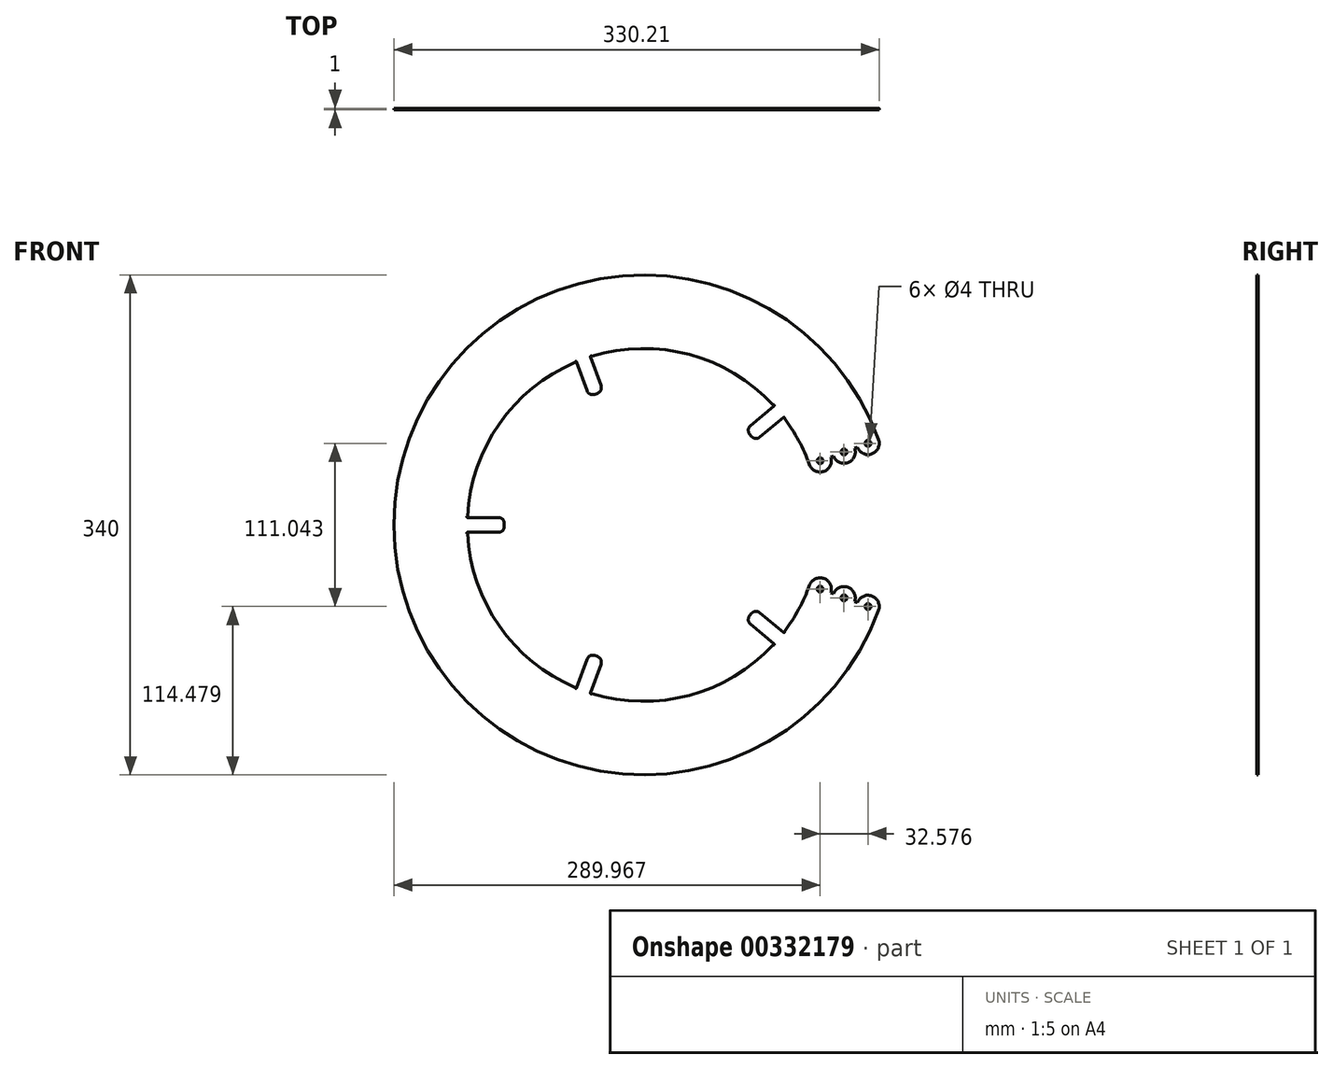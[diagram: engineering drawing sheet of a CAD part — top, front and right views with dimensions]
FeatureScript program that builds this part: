
annotation { "Feature Type Name" : "Feature", "Feature Type Description" : "" }
export const myFeature = defineFeature(function(context is Context, id is Id, definition is map)
    precondition{}
    {
        {
            var Q0;
            Q0=qCreatedBy(makeId("Front.planeOp"),FACE);
            var sketch = newSketch(context, id + "F0", { "sketchPlane" : qUnion([Q0])});
            skArc(sketch, "E0", {"start": v(112.76, 41.04) * mm, "mid": v(105.4, 57.38) * mm, "end": v(95.67, 72.44) * mm});
            skArc(sketch, "E1", {"start": v(159.75, 58.14) * mm, "mid": v(-170, 0) * mm, "end": v(159.75, -58.14) * mm});
            skLineSegment(sketch, "E2", {"start": v(0, 0) * mm, "end": v(-170, 0) * mm, "construction": true});
            skLineSegment(sketch, "E3", {"start": v(0, 0) * mm, "end": v(112.76, 41.04) * mm, "construction": true});
            skLineSegment(sketch, "E4", {"start": v(159.75, 58.14) * mm, "end": v(112.76, 41.04) * mm, "construction": true});
            skArc(sketch, "E5", {"start": v(112.76, 41.04) * mm, "mid": v(122.59, 36.46) * mm, "end": v(127.17, 46.29) * mm});
            skArc(sketch, "E6", {"start": v(129.05, 46.97) * mm, "mid": v(138.88, 42.39) * mm, "end": v(143.46, 52.22) * mm});
            skArc(sketch, "E7", {"start": v(159.75, 58.14) * mm, "mid": v(155.17, 48.32) * mm, "end": v(145.34, 52.9) * mm});
            skLineSegment(sketch, "E8", {"start": v(127.17, 46.29) * mm, "end": v(129.05, 46.97) * mm});
            skLineSegment(sketch, "E9", {"start": v(143.46, 52.22) * mm, "end": v(145.34, 52.9) * mm});
            skCircle(sketch, "E10", {"center": v(119.97, 43.66) * mm, "radius": 2 * mm});
            skCircle(sketch, "E11", {"center": v(136.26, 49.6) * mm, "radius": 2 * mm});
            skCircle(sketch, "E12", {"center": v(152.54, 55.52) * mm, "radius": 2 * mm});
            skLineSegment(sketch, "E13.MirrorCS", {"start": v(143.46, -52.22) * mm, "end": v(145.34, -52.9) * mm});
            skCircle(sketch, "E14.MirrorC", {"center": v(152.54, -55.52) * mm, "radius": 2 * mm});
            skCircle(sketch, "E15.MirrorC", {"center": v(136.26, -49.6) * mm, "radius": 2 * mm});
            skCircle(sketch, "E16.MirrorC", {"center": v(119.97, -43.66) * mm, "radius": 2 * mm});
            skLineSegment(sketch, "E17.MirrorCS", {"start": v(127.17, -46.29) * mm, "end": v(129.05, -46.97) * mm});
            skLineSegment(sketch, "E18.MirrorCS", {"start": v(159.75, -58.14) * mm, "end": v(112.76, -41.04) * mm, "construction": true});
            skArc(sketch, "E19.MirrorCS", {"start": v(159.75, -58.14) * mm, "mid": v(155.17, -48.32) * mm, "end": v(145.34, -52.9) * mm});
            skArc(sketch, "E20.MirrorCS", {"start": v(129.05, -46.97) * mm, "mid": v(138.88, -42.39) * mm, "end": v(143.46, -52.22) * mm});
            skArc(sketch, "E21.MirrorCS", {"start": v(112.76, -41.04) * mm, "mid": v(122.59, -36.46) * mm, "end": v(127.17, -46.29) * mm});
            skLineSegment(sketch, "E22", {"start": v(-119.9, 5) * mm, "end": v(-98.9, 5) * mm});
            skLineSegment(sketch, "E23", {"start": v(-94.9, 1) * mm, "end": v(-94.9, -1) * mm});
            skLineSegment(sketch, "E24", {"start": v(-98.9, -5) * mm, "end": v(-119.9, -5) * mm});
            skArc(sketch, "E25", {"start": v(-119.9, 5) * mm, "mid": v(-120.37, 5.52) * mm, "end": v(-119.85, 6) * mm});
            skArc(sketch, "E26.MirrorCS", {"start": v(-119.9, -5) * mm, "mid": v(-120.37, -5.52) * mm, "end": v(-119.85, -6) * mm});
            skPoint(sketch, "E27.visualSharp", {"position": v(-94.9, 5) * mm});
            skArc(sketch, "E27.filletArc", {"start": v(-94.9, 1) * mm, "mid": v(-96.07, 3.83) * mm, "end": v(-98.9, 5) * mm});
            skPoint(sketch, "E28.visualSharp", {"position": v(-94.9, -5) * mm});
            skArc(sketch, "E28.filletArc", {"start": v(-98.9, -5) * mm, "mid": v(-96.07, -3.83) * mm, "end": v(-94.9, -1) * mm});
            skLineSegment(sketch, "E29.1.0", {"start": v(-38.52, 91.22) * mm, "end": v(-45.7, 110.96) * mm});
            skPoint(sketch, "E29.1.1", {"position": v(-27.76, 90.88) * mm});
            skPoint(sketch, "E29.1.2", {"position": v(-37.15, 87.46) * mm});
            skLineSegment(sketch, "E29.1.3", {"start": v(-36.3, 114.38) * mm, "end": v(-29.13, 94.64) * mm});
            skLineSegment(sketch, "E29.1.4", {"start": v(-31.52, 89.51) * mm, "end": v(-33.4, 88.83) * mm});
            skArc(sketch, "E29.1.5", {"start": v(-38.52, 91.22) * mm, "mid": v(-36.45, 88.96) * mm, "end": v(-33.4, 88.83) * mm});
            skArc(sketch, "E29.1.6", {"start": v(-31.52, 89.51) * mm, "mid": v(-29.26, 91.58) * mm, "end": v(-29.13, 94.64) * mm});
            skArc(sketch, "E29.1.7", {"start": v(-45.7, 110.96) * mm, "mid": v(-46.36, 111.23) * mm, "end": v(-46.63, 110.57) * mm});
            skArc(sketch, "E29.1.8", {"start": v(-36.3, 114.38) * mm, "mid": v(-35.98, 115) * mm, "end": v(-35.35, 114.67) * mm});
            skLineSegment(sketch, "E29.2.0", {"start": v(72.54, 67.4) * mm, "end": v(88.63, 80.9) * mm});
            skPoint(sketch, "E29.2.1", {"position": v(75.9, 57.17) * mm});
            skPoint(sketch, "E29.2.2", {"position": v(69.48, 64.83) * mm});
            skLineSegment(sketch, "E29.2.3", {"start": v(95.06, 73.24) * mm, "end": v(78.97, 59.74) * mm});
            skLineSegment(sketch, "E29.2.4", {"start": v(73.34, 60.23) * mm, "end": v(72.05, 61.76) * mm});
            skArc(sketch, "E29.2.5", {"start": v(72.54, 67.4) * mm, "mid": v(71.13, 64.68) * mm, "end": v(72.05, 61.76) * mm});
            skArc(sketch, "E29.2.6", {"start": v(73.34, 60.23) * mm, "mid": v(76.05, 58.82) * mm, "end": v(78.97, 59.74) * mm});
            skArc(sketch, "E29.2.7", {"start": v(88.63, 80.9) * mm, "mid": v(88.66, 81.6) * mm, "end": v(87.95, 81.63) * mm});
            skArc(sketch, "E29.2.8", {"start": v(95.06, 73.24) * mm, "mid": v(95.76, 73.14) * mm, "end": v(95.67, 72.44) * mm});
            skLineSegment(sketch, "E29.anchor1", {"start": v(0, 0) * mm, "end": v(-119.85, -6) * mm, "construction": true});
            skLineSegment(sketch, "E29.anchor2", {"start": v(0, 0) * mm, "end": v(87.95, 81.63) * mm, "construction": true});
            skArc(sketch, "E30.trimOffspring", {"start": v(-46.63, 110.57) * mm, "mid": v(-98.3, 68.83) * mm, "end": v(-119.85, 6) * mm});
            skArc(sketch, "E31.trimOffspring", {"start": v(87.95, 81.63) * mm, "mid": v(31.06, 115.91) * mm, "end": v(-35.35, 114.67) * mm});
            skArc(sketch, "E32.MirrorCS", {"start": v(88.63, -80.9) * mm, "mid": v(88.66, -81.6) * mm, "end": v(87.95, -81.63) * mm});
            skArc(sketch, "E33.MirrorCS", {"start": v(-45.7, -110.96) * mm, "mid": v(-46.36, -111.23) * mm, "end": v(-46.63, -110.57) * mm});
            skArc(sketch, "E34.MirrorCS", {"start": v(-36.3, -114.38) * mm, "mid": v(-35.98, -115) * mm, "end": v(-35.35, -114.67) * mm});
            skLineSegment(sketch, "E35.MirrorCS", {"start": v(73.34, -60.23) * mm, "end": v(72.05, -61.76) * mm});
            skArc(sketch, "E36.MirrorCS", {"start": v(95.06, -73.24) * mm, "mid": v(95.76, -73.14) * mm, "end": v(95.67, -72.44) * mm});
            skArc(sketch, "E37.MirrorCS", {"start": v(-38.52, -91.22) * mm, "mid": v(-36.45, -88.96) * mm, "end": v(-33.4, -88.83) * mm});
            skLineSegment(sketch, "E38.MirrorCS", {"start": v(-31.52, -89.51) * mm, "end": v(-33.4, -88.83) * mm});
            skArc(sketch, "E39.MirrorCS", {"start": v(73.34, -60.23) * mm, "mid": v(76.05, -58.82) * mm, "end": v(78.97, -59.74) * mm});
            skArc(sketch, "E40.MirrorCS", {"start": v(72.54, -67.4) * mm, "mid": v(71.13, -64.68) * mm, "end": v(72.05, -61.76) * mm});
            skArc(sketch, "E41.MirrorCS", {"start": v(-31.52, -89.51) * mm, "mid": v(-29.26, -91.58) * mm, "end": v(-29.13, -94.64) * mm});
            skLineSegment(sketch, "E42.MirrorCS", {"start": v(72.54, -67.4) * mm, "end": v(88.63, -80.9) * mm});
            skLineSegment(sketch, "E43.MirrorCS", {"start": v(95.06, -73.24) * mm, "end": v(78.97, -59.74) * mm});
            skPoint(sketch, "E44.MirrorP", {"position": v(69.48, -64.83) * mm});
            skPoint(sketch, "E45.MirrorP", {"position": v(75.9, -57.17) * mm});
            skLineSegment(sketch, "E46.MirrorCS", {"start": v(-38.52, -91.22) * mm, "end": v(-45.7, -110.96) * mm});
            skPoint(sketch, "E47.MirrorP", {"position": v(-37.15, -87.46) * mm});
            skArc(sketch, "E48.MirrorCS", {"start": v(87.95, -81.63) * mm, "mid": v(31.06, -115.91) * mm, "end": v(-35.35, -114.67) * mm});
            skLineSegment(sketch, "E49.MirrorCS", {"start": v(-36.3, -114.38) * mm, "end": v(-29.13, -94.64) * mm});
            skPoint(sketch, "E50.MirrorP", {"position": v(-27.76, -90.88) * mm});
            skArc(sketch, "E51.MirrorCS", {"start": v(112.76, -41.04) * mm, "mid": v(105.4, -57.38) * mm, "end": v(95.67, -72.44) * mm});
            skArc(sketch, "E52.MirrorCS", {"start": v(-46.63, -110.57) * mm, "mid": v(-98.3, -68.83) * mm, "end": v(-119.85, -6) * mm});
            skSolve(sketch);
        }
        {
            var Q0;
            Q0 = qSketchRegion(id + "F0", true);
            extrude(context, id + "F1", {"entities" : qUnion([Q0]), "depth" : 1 * mm});
        }
    });
